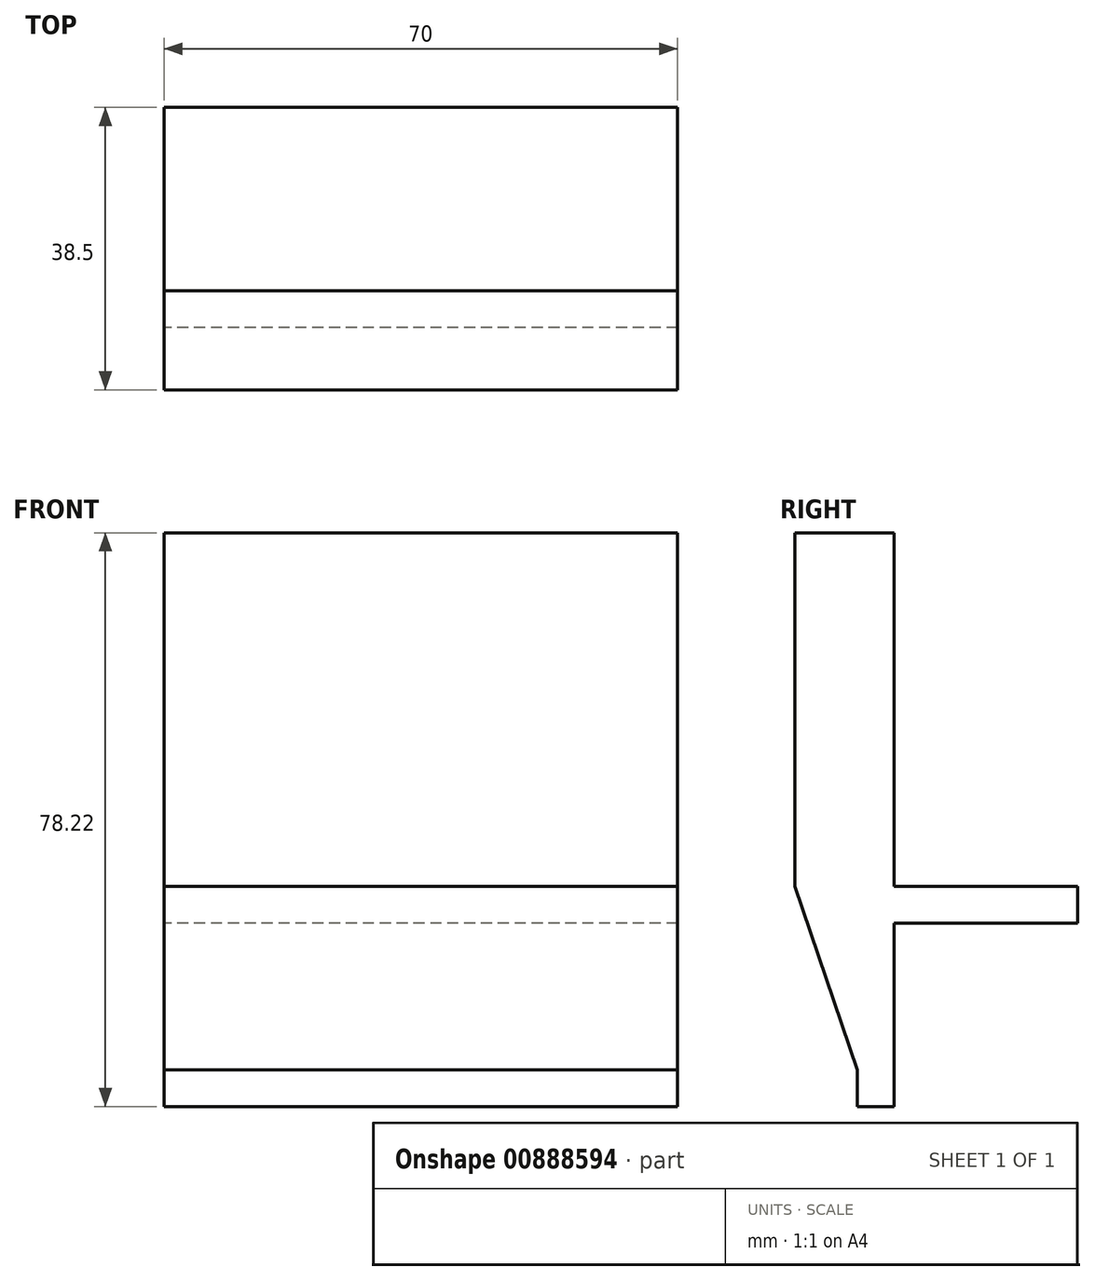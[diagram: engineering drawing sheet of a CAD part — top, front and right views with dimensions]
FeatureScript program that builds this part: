
annotation { "Feature Type Name" : "Feature", "Feature Type Description" : "" }
export const myFeature = defineFeature(function(context is Context, id is Id, definition is map)
    precondition{}
    {
        {
            var Q0;
            Q0=qCreatedBy(makeId("Right.planeOp"),FACE);
            var sketch = newSketch(context, id + "F0", { "sketchPlane" : qUnion([Q0])});
            skLineSegment(sketch, "E0", {"start": v(0, 0) * mm, "end": v(0, 26.1) * mm});
            skLineSegment(sketch, "E1", {"start": v(0, 26.1) * mm, "end": v(13.5, 26.1) * mm});
            skLineSegment(sketch, "E2", {"start": v(13.5, 26.1) * mm, "end": v(13.5, -10.9) * mm});
            skLineSegment(sketch, "E3", {"start": v(13.5, 8.03) * mm, "end": v(13.5, -5.72) * mm});
            skLineSegment(sketch, "E4", {"start": v(13.5, -10.9) * mm, "end": v(33.5, -10.9) * mm});
            skLineSegment(sketch, "E5", {"start": v(33.5, -10.9) * mm, "end": v(33.5, -15.9) * mm});
            skLineSegment(sketch, "E6", {"start": v(33.5, -15.9) * mm, "end": v(13.5, -15.9) * mm});
            skLineSegment(sketch, "E7", {"start": v(13.5, -15.9) * mm, "end": v(13.5, -35.9) * mm});
            skLineSegment(sketch, "E8", {"start": v(13.5, -35.9) * mm, "end": v(8.5, -35.9) * mm});
            skLineSegment(sketch, "E9", {"start": v(8.5, -35.9) * mm, "end": v(0, -10.9) * mm});
            skLineSegment(sketch, "E10", {"start": v(0, -10.9) * mm, "end": v(0, 0) * mm});
            skSolve(sketch);
        }
        {
            var Q0;
            Q0 = qSketchRegion(id + "F0", true);
            extrude(context, id + "F1", {"entities" : qUnion([Q0]), "depth" : 70 * mm, "offsetDistance" : 25 * mm});
        }
        {
            var Q0;
            Q0=makeQuery(id+"F1.opExtrude","SWEPT_FACE",FACE,{"disambiguationData":[OSD([sQuery(id+"F0.wireOp",EDGE,"E1")])]});
            extrude(context, id + "F2", {"entities" : qUnion([Q0]), "operationType" : NewBodyOperationType.ADD, "depth" : 5 * mm, "offsetDistance" : 25 * mm});
        }
        {
            var Q0;
            Q0=makeQuery(id+"F1.opExtrude","SWEPT_FACE",FACE,{"disambiguationData":[OSD([sQuery(id+"F0.wireOp",EDGE,"E2"),sQuery(id+"F0.wireOp",EDGE,"E3")])]});
            var sketch = newSketch(context, id + "F3", { "sketchPlane" : qUnion([Q0])});
            skLineSegment(sketch, "E11", {"start": v(-70, -10.9) * mm, "end": v(-70, -6.92) * mm});
            skLineSegment(sketch, "E12", {"start": v(-35, 31.1) * mm, "end": v(-40, 31.1) * mm});
            skLineSegment(sketch, "E13", {"start": v(-35, 31.1) * mm, "end": v(-30, 31.1) * mm});
            skPoint(sketch, "E14.visualSharp", {"position": v(-70, -4.33) * mm});
            skArc(sketch, "E14.filletArc", {"start": v(-68.41, -2.3) * mm, "mid": v(-69.6, -4.48) * mm, "end": v(-70, -6.92) * mm});
            skLineSegment(sketch, "E15", {"start": v(0, -6.92) * mm, "end": v(0, -10.9) * mm});
            skPoint(sketch, "E16.visualSharp", {"position": v(0, -4.33) * mm});
            skArc(sketch, "E16.filletArc", {"start": v(0, -6.92) * mm, "mid": v(-0.4, -4.48) * mm, "end": v(-1.59, -2.3) * mm});
            skLineSegment(sketch, "E17", {"start": v(-70, -10.9) * mm, "end": v(-70, 31.1) * mm});
            skLineSegment(sketch, "E18", {"start": v(-70, -10.9) * mm, "end": v(-70, 37.32) * mm});
            skLineSegment(sketch, "E19", {"start": v(-70, 37.32) * mm, "end": v(0, 37.32) * mm});
            skLineSegment(sketch, "E20", {"start": v(0, 37.32) * mm, "end": v(0, -10.9) * mm});
            skLineSegment(sketch, "E21", {"start": v(-70, -10.9) * mm, "end": v(0, -10.9) * mm});
            skSolve(sketch);
        }
        {
            var Q0;
            {var subQ3=sQuery(id+"F3.wireOp",EDGE,"E12");Q0=makeQuery(id+"F3.imprint","IMPRINT",FACE,{"disambiguationData":[TD([[makeQuery(id+"F3.imprint","IMPRINT",EDGE,{"derivedFrom":subQ3}),-1.0]])]});}
            var Q1;
            {var subQ3=sQuery(id+"F3.wireOp",EDGE,"E13");Q1=makeQuery(id+"F3.imprint","IMPRINT",FACE,{"disambiguationData":[TD([[makeQuery(id+"F3.imprint","IMPRINT",EDGE,{"derivedFrom":subQ3}),-1.0]])]});}
            extrude(context, id + "F4", {"entities" : qUnion([Q0, Q1]), "operationType" : NewBodyOperationType.REMOVE, "oppositeDirection" : true, "depth" : 25 * mm, "offsetDistance" : 25 * mm});
        }
        {
            var Q0;
            Q0=makeQuery(id+"F1.opExtrude","SWEPT_FACE",FACE,{"disambiguationData":[OSD([sQuery(id+"F0.wireOp",EDGE,"E5")])]});
            extrude(context, id + "F5", {"entities" : qUnion([Q0]), "operationType" : NewBodyOperationType.ADD, "depth" : 5 * mm, "offsetDistance" : 25 * mm});
        }
        {
            var Q0;
            Q0=makeQuery(id+"F1.opExtrude","SWEPT_FACE",FACE,{"disambiguationData":[OSD([sQuery(id+"F0.wireOp",EDGE,"E8")])]});
            extrude(context, id + "F6", {"entities" : qUnion([Q0]), "operationType" : NewBodyOperationType.ADD, "depth" : 5 * mm, "offsetDistance" : 25 * mm});
        }
        {
            var Q0;
            Q0 = qSketchRegion(id + "F3", true);
            extrude(context, id + "F7", {"entities" : qUnion([Q0]), "operationType" : NewBodyOperationType.ADD, "oppositeDirection" : true, "depth" : 13.5 * mm, "offsetDistance" : 25 * mm});
        }
    });
